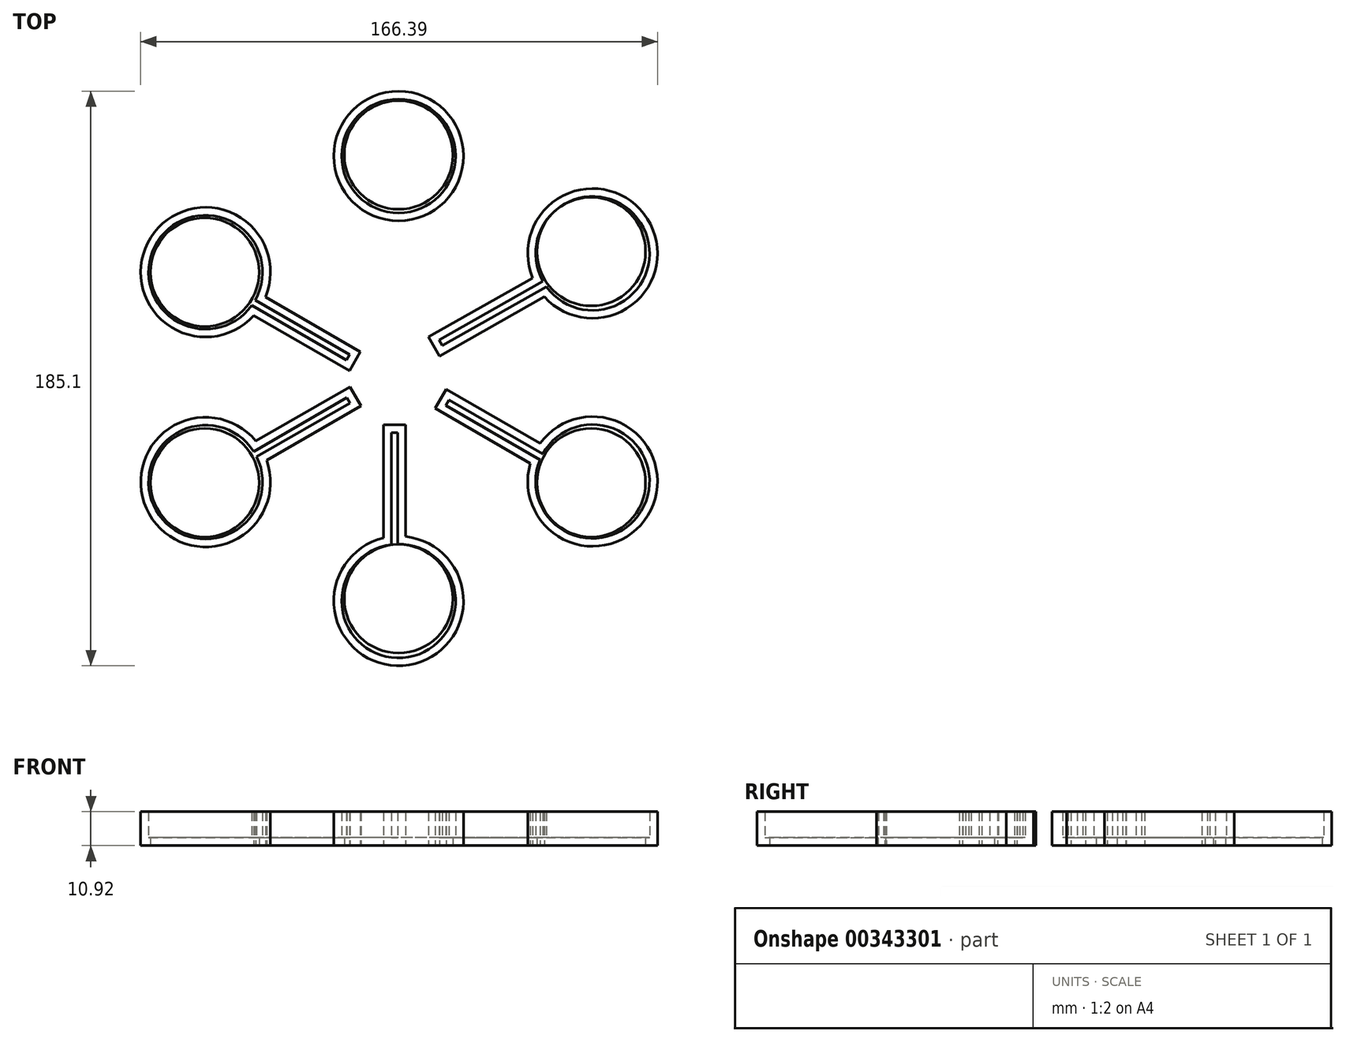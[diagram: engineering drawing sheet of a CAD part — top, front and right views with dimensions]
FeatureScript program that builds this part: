
annotation { "Feature Type Name" : "Feature", "Feature Type Description" : "" }
export const myFeature = defineFeature(function(context is Context, id is Id, definition is map)
    precondition{}
    {
        {
            var Q0;
            Q0=qCreatedBy(makeId("Top.planeOp"),FACE);
            var sketch = newSketch(context, id + "F0", { "sketchPlane" : qUnion([Q0])});
            skLineSegment(sketch, "E0.bottom", {"start": v(-4.9, 14.96) * mm, "end": v(2.2, 14.96) * mm});
            skLineSegment(sketch, "E0.top", {"start": v(-4.9, 63.67) * mm, "end": v(2.2, 63.67) * mm});
            skLineSegment(sketch, "E0.left", {"start": v(-4.9, 14.96) * mm, "end": v(-4.9, 63.67) * mm});
            skLineSegment(sketch, "E0.right", {"start": v(2.2, 14.96) * mm, "end": v(2.2, 63.67) * mm});
            skLineSegment(sketch, "E1.MirrorCS", {"start": v(2.2, -14.96) * mm, "end": v(2.2, -63.67) * mm});
            skLineSegment(sketch, "E2.MirrorCS", {"start": v(-4.9, -14.96) * mm, "end": v(-4.9, -63.67) * mm});
            skLineSegment(sketch, "E3.MirrorCS", {"start": v(-4.9, -63.67) * mm, "end": v(2.2, -63.67) * mm});
            skLineSegment(sketch, "E4", {"start": v(-12.3, 8.6) * mm, "end": v(-54.48, 32.97) * mm});
            skLineSegment(sketch, "E5", {"start": v(-54.48, 32.97) * mm, "end": v(-58.03, 26.83) * mm});
            skLineSegment(sketch, "E6", {"start": v(-58.03, 26.83) * mm, "end": v(-15.86, 2.47) * mm});
            skLineSegment(sketch, "E7", {"start": v(-15.72, -2.7) * mm, "end": v(-57.9, -27.03) * mm});
            skLineSegment(sketch, "E8", {"start": v(-57.9, -27.03) * mm, "end": v(-54.37, -33.17) * mm});
            skLineSegment(sketch, "E9", {"start": v(-54.37, -33.17) * mm, "end": v(-12.18, -8.84) * mm});
            skLineSegment(sketch, "E10", {"start": v(9.56, 13.37) * mm, "end": v(51.98, 37.3) * mm});
            skLineSegment(sketch, "E11", {"start": v(51.98, 37.3) * mm, "end": v(55.46, 31.13) * mm});
            skLineSegment(sketch, "E12", {"start": v(55.46, 31.13) * mm, "end": v(13.1, 7.22) * mm});
            skLineSegment(sketch, "E13", {"start": v(11.74, -9.6) * mm, "end": v(53.91, -33.96) * mm});
            skLineSegment(sketch, "E14", {"start": v(53.91, -33.96) * mm, "end": v(57.46, -27.82) * mm});
            skLineSegment(sketch, "E15", {"start": v(57.46, -27.82) * mm, "end": v(15.29, -3.45) * mm});
            skCircle(sketch, "E16", {"center": v(-62.17, 34.25) * mm, "radius": 20.89 * mm});
            skCircle(sketch, "E17", {"center": v(-62.17, -33.39) * mm, "radius": 20.89 * mm});
            skCircle(sketch, "E18", {"center": v(62.45, -33.17) * mm, "radius": 20.89 * mm});
            skCircle(sketch, "E19", {"center": v(62.45, 40.3) * mm, "radius": 20.89 * mm});
            skCircle(sketch, "E20", {"center": v(0, 71.66) * mm, "radius": 20.89 * mm});
            skCircle(sketch, "E21", {"center": v(0, -71.66) * mm, "radius": 20.89 * mm});
            skLineSegment(sketch, "E22", {"start": v(-4.9, -14.96) * mm, "end": v(2.2, -14.96) * mm});
            skLineSegment(sketch, "E23", {"start": v(11.74, -9.6) * mm, "end": v(15.29, -3.45) * mm});
            skLineSegment(sketch, "E24", {"start": v(13.1, 7.22) * mm, "end": v(9.56, 13.37) * mm});
            skLineSegment(sketch, "E25", {"start": v(2.2, 14.96) * mm, "end": v(-4.9, 14.96) * mm});
            skLineSegment(sketch, "E26", {"start": v(-12.3, 8.6) * mm, "end": v(-15.86, 2.47) * mm});
            skLineSegment(sketch, "E27", {"start": v(-15.72, -2.7) * mm, "end": v(-12.18, -8.84) * mm});
            skSolve(sketch);
        }
        {
            var Q0;
            {var subQ0=sQuery(id+"F0.wireOp",EDGE,"E5");Q0=makeQuery(id+"F0.imprint","IMPRINT",FACE,{"disambiguationData":[TD([[makeQuery(id+"F0.imprint","IMPRINT",EDGE,{"derivedFrom":subQ0}),-1.0]])]});}
            var Q1;
            {var subQ0=sQuery(id+"F0.wireOp",EDGE,"E26");Q1=makeQuery(id+"F0.imprint","IMPRINT",FACE,{"disambiguationData":[TD([[makeQuery(id+"F0.imprint","IMPRINT",EDGE,{"derivedFrom":subQ0}),-1.0]])]});}
            var Q2;
            {var subQ0=sQuery(id+"F0.wireOp",EDGE,"E5");Q2=makeQuery(id+"F0.imprint","IMPRINT",FACE,{"disambiguationData":[TD([[makeQuery(id+"F0.imprint","IMPRINT",EDGE,{"derivedFrom":subQ0}),1.0]])]});}
            var Q3;
            {var subQ0=sQuery(id+"F0.wireOp",EDGE,"E0.top");Q3=makeQuery(id+"F0.imprint","IMPRINT",FACE,{"disambiguationData":[TD([[makeQuery(id+"F0.imprint","IMPRINT",EDGE,{"derivedFrom":subQ0}),1.0]])]});}
            var Q4;
            {var subQ0=sQuery(id+"F0.wireOp",EDGE,"E0.top");Q4=makeQuery(id+"F0.imprint","IMPRINT",FACE,{"disambiguationData":[TD([[makeQuery(id+"F0.imprint","IMPRINT",EDGE,{"derivedFrom":subQ0}),-1.0]])]});}
            var Q5;
            {var subQ0=sQuery(id+"F0.wireOp",EDGE,"E25");Q5=makeQuery(id+"F0.imprint","IMPRINT",FACE,{"disambiguationData":[TD([[makeQuery(id+"F0.imprint","IMPRINT",EDGE,{"derivedFrom":subQ0}),-1.0]])]});}
            var Q6;
            {var subQ0=sQuery(id+"F0.wireOp",EDGE,"E24");Q6=makeQuery(id+"F0.imprint","IMPRINT",FACE,{"disambiguationData":[TD([[makeQuery(id+"F0.imprint","IMPRINT",EDGE,{"derivedFrom":subQ0}),-1.0]])]});}
            var Q7;
            {var subQ0=sQuery(id+"F0.wireOp",EDGE,"E11");Q7=makeQuery(id+"F0.imprint","IMPRINT",FACE,{"disambiguationData":[TD([[makeQuery(id+"F0.imprint","IMPRINT",EDGE,{"derivedFrom":subQ0}),1.0]])]});}
            var Q8;
            {var subQ0=sQuery(id+"F0.wireOp",EDGE,"E11");Q8=makeQuery(id+"F0.imprint","IMPRINT",FACE,{"disambiguationData":[TD([[makeQuery(id+"F0.imprint","IMPRINT",EDGE,{"derivedFrom":subQ0}),-1.0]])]});}
            var Q9;
            {var subQ0=sQuery(id+"F0.wireOp",EDGE,"E23");Q9=makeQuery(id+"F0.imprint","IMPRINT",FACE,{"disambiguationData":[TD([[makeQuery(id+"F0.imprint","IMPRINT",EDGE,{"derivedFrom":subQ0}),-1.0]])]});}
            var Q10;
            {var subQ0=sQuery(id+"F0.wireOp",EDGE,"E14");Q10=makeQuery(id+"F0.imprint","IMPRINT",FACE,{"disambiguationData":[TD([[makeQuery(id+"F0.imprint","IMPRINT",EDGE,{"derivedFrom":subQ0}),-1.0]])]});}
            var Q11;
            {var subQ0=sQuery(id+"F0.wireOp",EDGE,"E14");Q11=makeQuery(id+"F0.imprint","IMPRINT",FACE,{"disambiguationData":[TD([[makeQuery(id+"F0.imprint","IMPRINT",EDGE,{"derivedFrom":subQ0}),1.0]])]});}
            var Q12;
            {var subQ0=sQuery(id+"F0.wireOp",EDGE,"E3.MirrorCS");Q12=makeQuery(id+"F0.imprint","IMPRINT",FACE,{"disambiguationData":[TD([[makeQuery(id+"F0.imprint","IMPRINT",EDGE,{"derivedFrom":subQ0}),-1.0]])]});}
            var Q13;
            {var subQ0=sQuery(id+"F0.wireOp",EDGE,"E3.MirrorCS");Q13=makeQuery(id+"F0.imprint","IMPRINT",FACE,{"disambiguationData":[TD([[makeQuery(id+"F0.imprint","IMPRINT",EDGE,{"derivedFrom":subQ0}),1.0]])]});}
            var Q14;
            {var subQ0=sQuery(id+"F0.wireOp",EDGE,"E22");Q14=makeQuery(id+"F0.imprint","IMPRINT",FACE,{"disambiguationData":[TD([[makeQuery(id+"F0.imprint","IMPRINT",EDGE,{"derivedFrom":subQ0}),-1.0]])]});}
            var Q15;
            {var subQ0=sQuery(id+"F0.wireOp",EDGE,"E8");Q15=makeQuery(id+"F0.imprint","IMPRINT",FACE,{"disambiguationData":[TD([[makeQuery(id+"F0.imprint","IMPRINT",EDGE,{"derivedFrom":subQ0}),-1.0]])]});}
            var Q16;
            {var subQ0=sQuery(id+"F0.wireOp",EDGE,"E27");Q16=makeQuery(id+"F0.imprint","IMPRINT",FACE,{"disambiguationData":[TD([[makeQuery(id+"F0.imprint","IMPRINT",EDGE,{"derivedFrom":subQ0}),-1.0]])]});}
            var Q17;
            {var subQ0=sQuery(id+"F0.wireOp",EDGE,"E8");Q17=makeQuery(id+"F0.imprint","IMPRINT",FACE,{"disambiguationData":[TD([[makeQuery(id+"F0.imprint","IMPRINT",EDGE,{"derivedFrom":subQ0}),1.0]])]});}
            extrude(context, id + "F1", {"entities" : qUnion([Q0, Q1, Q2, Q3, Q4, Q5, Q6, Q7, Q8, Q9, Q10, Q11, Q12, Q13, Q14, Q15, Q16, Q17]), "depth" : 10.92 * mm});
        }
        {
            var Q0;
            Q0=makeQuery(id+"F1.opExtrude","CAP_FACE",FACE,{"disambiguationData":[OSD([sQuery(id+"F0.wireOp",EDGE,"E13"),sQuery(id+"F0.wireOp",EDGE,"E15"),sQuery(id+"F0.wireOp",EDGE,"E18"),sQuery(id+"F0.wireOp",EDGE,"E23")])],"isStart":false});
            var Q1;
            Q1=makeQuery(id+"F1.opExtrude","CAP_FACE",FACE,{"disambiguationData":[OSD([sQuery(id+"F0.wireOp",EDGE,"E1.MirrorCS"),sQuery(id+"F0.wireOp",EDGE,"E2.MirrorCS"),sQuery(id+"F0.wireOp",EDGE,"E21"),sQuery(id+"F0.wireOp",EDGE,"E22")])],"isStart":false});
            var Q2;
            Q2=makeQuery(id+"F1.opExtrude","CAP_FACE",FACE,{"disambiguationData":[OSD([sQuery(id+"F0.wireOp",EDGE,"E7"),sQuery(id+"F0.wireOp",EDGE,"E9"),sQuery(id+"F0.wireOp",EDGE,"E17"),sQuery(id+"F0.wireOp",EDGE,"E27")])],"isStart":false});
            var Q3;
            Q3=makeQuery(id+"F1.opExtrude","CAP_FACE",FACE,{"disambiguationData":[OSD([sQuery(id+"F0.wireOp",EDGE,"E4"),sQuery(id+"F0.wireOp",EDGE,"E6"),sQuery(id+"F0.wireOp",EDGE,"E16"),sQuery(id+"F0.wireOp",EDGE,"E26")])],"isStart":false});
            var Q4;
            Q4=makeQuery(id+"F1.opExtrude","CAP_FACE",FACE,{"disambiguationData":[OSD([sQuery(id+"F0.wireOp",EDGE,"E0.left"),sQuery(id+"F0.wireOp",EDGE,"E0.right"),sQuery(id+"F0.wireOp",EDGE,"E20"),sQuery(id+"F0.wireOp",EDGE,"E25")])],"isStart":false});
            var Q5;
            Q5=makeQuery(id+"F1.opExtrude","CAP_FACE",FACE,{"disambiguationData":[OSD([sQuery(id+"F0.wireOp",EDGE,"E10"),sQuery(id+"F0.wireOp",EDGE,"E12"),sQuery(id+"F0.wireOp",EDGE,"E19"),sQuery(id+"F0.wireOp",EDGE,"E24")])],"isStart":false});
            shell(context, id + "F2", {"entities" : qUnion([Q0, Q1, Q2, Q3, Q4, Q5]), "thickness" : 2.54 * mm});
        }
        {
            var Q0;
            Q0=qCreatedBy(makeId("Top.planeOp"),FACE);
            var sketch = newSketch(context, id + "F3", { "sketchPlane" : qUnion([Q0])});
            skCircle(sketch, "E28", {"center": v(0, 72) * mm, "radius": 17.75 * mm});
            skCircle(sketch, "E29", {"center": v(0, -70.96) * mm, "radius": 17.33 * mm});
            skCircle(sketch, "E30", {"center": v(-62.43, -33.56) * mm, "radius": 18.4 * mm});
            skCircle(sketch, "E31", {"center": v(-62.43, 34.26) * mm, "radius": 18.06 * mm});
            skCircle(sketch, "E32", {"center": v(62.01, -33.56) * mm, "radius": 17.6 * mm});
            skCircle(sketch, "E33", {"center": v(62.01, 40.9) * mm, "radius": 17.69 * mm});
            skSolve(sketch);
        }
        {
            var Q0;
            Q0=sQuery(id+"F3.wireOp",VERTEX,"E31.center");
            var Q1;
            Q1=sQuery(id+"F3.wireOp",VERTEX,"E28.center");
            var Q2;
            Q2=sQuery(id+"F3.wireOp",VERTEX,"E33.center");
            var Q3;
            Q3=sQuery(id+"F3.wireOp",VERTEX,"E32.center");
            var Q4;
            Q4=sQuery(id+"F3.wireOp",VERTEX,"E29.center");
            var Q5;
            Q5=sQuery(id+"F3.wireOp",VERTEX,"E30.center");
            var Q6;
            Q6=makeQuery(id+"F1.opExtrude","SWEPT_BODY",BODY,{"disambiguationData":[OSD([sQuery(id+"F0.wireOp",EDGE,"E4"),sQuery(id+"F0.wireOp",EDGE,"E6"),sQuery(id+"F0.wireOp",EDGE,"E16"),sQuery(id+"F0.wireOp",EDGE,"E26")])]});
            var Q7;
            Q7=makeQuery(id+"F1.opExtrude","SWEPT_BODY",BODY,{"disambiguationData":[OSD([sQuery(id+"F0.wireOp",EDGE,"E0.left"),sQuery(id+"F0.wireOp",EDGE,"E0.right"),sQuery(id+"F0.wireOp",EDGE,"E20"),sQuery(id+"F0.wireOp",EDGE,"E25")])]});
            var Q8;
            Q8=makeQuery(id+"F1.opExtrude","SWEPT_BODY",BODY,{"disambiguationData":[OSD([sQuery(id+"F0.wireOp",EDGE,"E10"),sQuery(id+"F0.wireOp",EDGE,"E12"),sQuery(id+"F0.wireOp",EDGE,"E19"),sQuery(id+"F0.wireOp",EDGE,"E24")])]});
            var Q9;
            Q9=makeQuery(id+"F1.opExtrude","SWEPT_BODY",BODY,{"disambiguationData":[OSD([sQuery(id+"F0.wireOp",EDGE,"E13"),sQuery(id+"F0.wireOp",EDGE,"E15"),sQuery(id+"F0.wireOp",EDGE,"E18"),sQuery(id+"F0.wireOp",EDGE,"E23")])]});
            var Q10;
            Q10=makeQuery(id+"F1.opExtrude","SWEPT_BODY",BODY,{"disambiguationData":[OSD([sQuery(id+"F0.wireOp",EDGE,"E1.MirrorCS"),sQuery(id+"F0.wireOp",EDGE,"E2.MirrorCS"),sQuery(id+"F0.wireOp",EDGE,"E21"),sQuery(id+"F0.wireOp",EDGE,"E22")])]});
            var Q11;
            Q11=makeQuery(id+"F1.opExtrude","SWEPT_BODY",BODY,{"disambiguationData":[OSD([sQuery(id+"F0.wireOp",EDGE,"E7"),sQuery(id+"F0.wireOp",EDGE,"E9"),sQuery(id+"F0.wireOp",EDGE,"E17"),sQuery(id+"F0.wireOp",EDGE,"E27")])]});
            hole(context, id + "F4", {"style" : HoleStyle.SIMPLE, "endStyle" : HoleEndStyle.THROUGH, "oppositeDirection" : true, "holeDiameter" : 35 * mm, "isTappedThrough" : true, "tappedDepth" : 12 * mm, "tapClearance" : 3, "locations" : qUnion([Q0, Q1, Q2, Q3, Q4, Q5]), "scope" : qUnion([Q6, Q7, Q8, Q9, Q10, Q11])});
        }
    });
